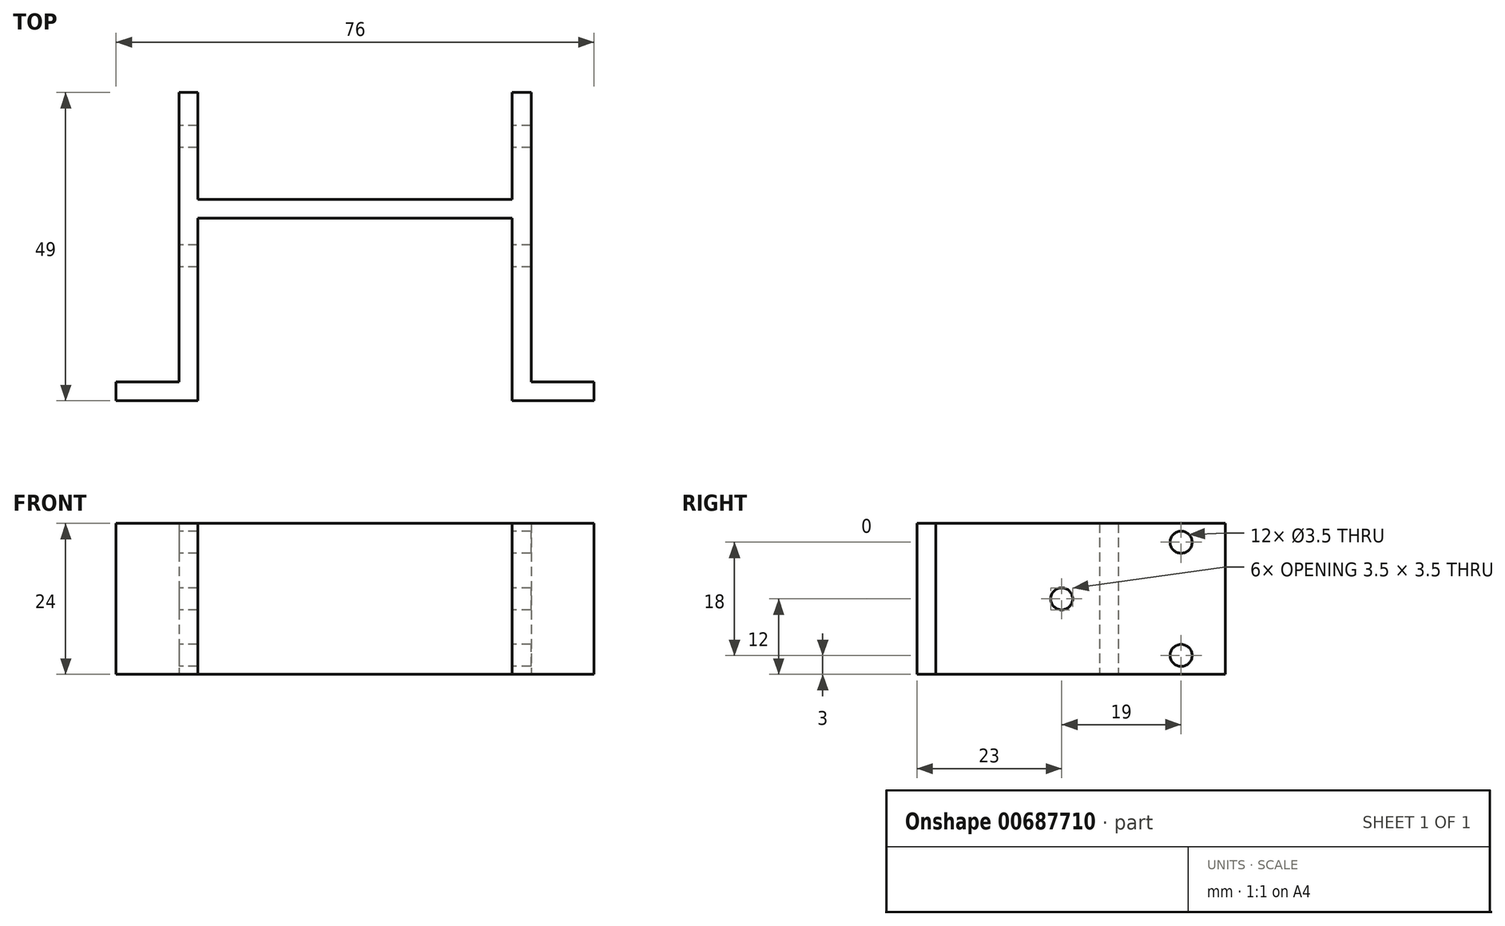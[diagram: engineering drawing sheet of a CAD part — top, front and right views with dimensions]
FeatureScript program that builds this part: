
annotation { "Feature Type Name" : "Feature", "Feature Type Description" : "" }
export const myFeature = defineFeature(function(context is Context, id is Id, definition is map)
    precondition{}
    {
        {
            var Q0;
            Q0=qCreatedBy(makeId("Top.planeOp"),FACE);
            var sketch = newSketch(context, id + "F0", { "sketchPlane" : qUnion([Q0])});
            skLineSegment(sketch, "E0", {"start": v(-38, 0) * mm, "end": v(-25, 0) * mm});
            skLineSegment(sketch, "E1", {"start": v(-38, 0) * mm, "end": v(-38, 3) * mm});
            skLineSegment(sketch, "E2", {"start": v(-38, 3) * mm, "end": v(-28, 3) * mm});
            skLineSegment(sketch, "E3", {"start": v(-28, 3) * mm, "end": v(-28, 49) * mm});
            skLineSegment(sketch, "E4", {"start": v(-28, 49) * mm, "end": v(-25, 49) * mm});
            skLineSegment(sketch, "E5", {"start": v(-25, 49) * mm, "end": v(-25, 32) * mm});
            skLineSegment(sketch, "E6", {"start": v(-25, 32) * mm, "end": v(25, 32) * mm});
            skLineSegment(sketch, "E7", {"start": v(25, 32) * mm, "end": v(25, 49) * mm});
            skLineSegment(sketch, "E8", {"start": v(25, 49) * mm, "end": v(28, 49) * mm});
            skLineSegment(sketch, "E9", {"start": v(28, 49) * mm, "end": v(28, 3) * mm});
            skLineSegment(sketch, "E10", {"start": v(28, 3) * mm, "end": v(38, 3) * mm});
            skLineSegment(sketch, "E11", {"start": v(38, 3) * mm, "end": v(38, 0) * mm});
            skLineSegment(sketch, "E12", {"start": v(38, 0) * mm, "end": v(25, 0) * mm});
            skLineSegment(sketch, "E13", {"start": v(25, 0) * mm, "end": v(25, 29) * mm});
            skLineSegment(sketch, "E14", {"start": v(25, 29) * mm, "end": v(-25, 29) * mm});
            skLineSegment(sketch, "E15", {"start": v(-25, 29) * mm, "end": v(-25, 0) * mm});
            skSolve(sketch);
        }
        {
            var Q0;
            Q0 = qSketchRegion(id + "F0", true);
            extrude(context, id + "F1", {"entities" : qUnion([Q0]), "endBound" : BoundingType.SYMMETRIC, "depth" : 24 * mm, "offsetDistance" : 25 * mm});
        }
        {
            var Q0;
            Q0=makeQuery(id+"F1.opExtrude","SWEPT_FACE",FACE,{"disambiguationData":[OSD([sQuery(id+"F0.wireOp",EDGE,"E3")])]});
            var sketch = newSketch(context, id + "F2", { "sketchPlane" : qUnion([Q0])});
            skCircle(sketch, "E16", {"center": v(-42, 9) * mm, "radius": 1.75 * mm});
            skCircle(sketch, "E17", {"center": v(-42, -9) * mm, "radius": 1.75 * mm});
            skCircle(sketch, "E18", {"center": v(-23, 0) * mm, "radius": 1.75 * mm});
            skLineSegment(sketch, "E19.0.1", {"start": v(-29, -12) * mm, "end": v(-29, 12) * mm});
            skLineSegment(sketch, "E19.0.3", {"start": v(-29, 12) * mm, "end": v(-29, -12) * mm});
            skLineSegment(sketch, "E20.0.1", {"start": v(-32, -12) * mm, "end": v(-32, 12) * mm});
            skLineSegment(sketch, "E20.0.3", {"start": v(-32, 12) * mm, "end": v(-32, -12) * mm});
            skSolve(sketch);
        }
        {
            var Q0;
            Q0 = qSketchRegion(id + "F2", true);
            extrude(context, id + "F3", {"entities" : qUnion([Q0]), "operationType" : NewBodyOperationType.REMOVE, "endBound" : BoundingType.THROUGH_ALL, "oppositeDirection" : true, "depth" : 25 * mm, "offsetDistance" : 25 * mm});
        }
    });
